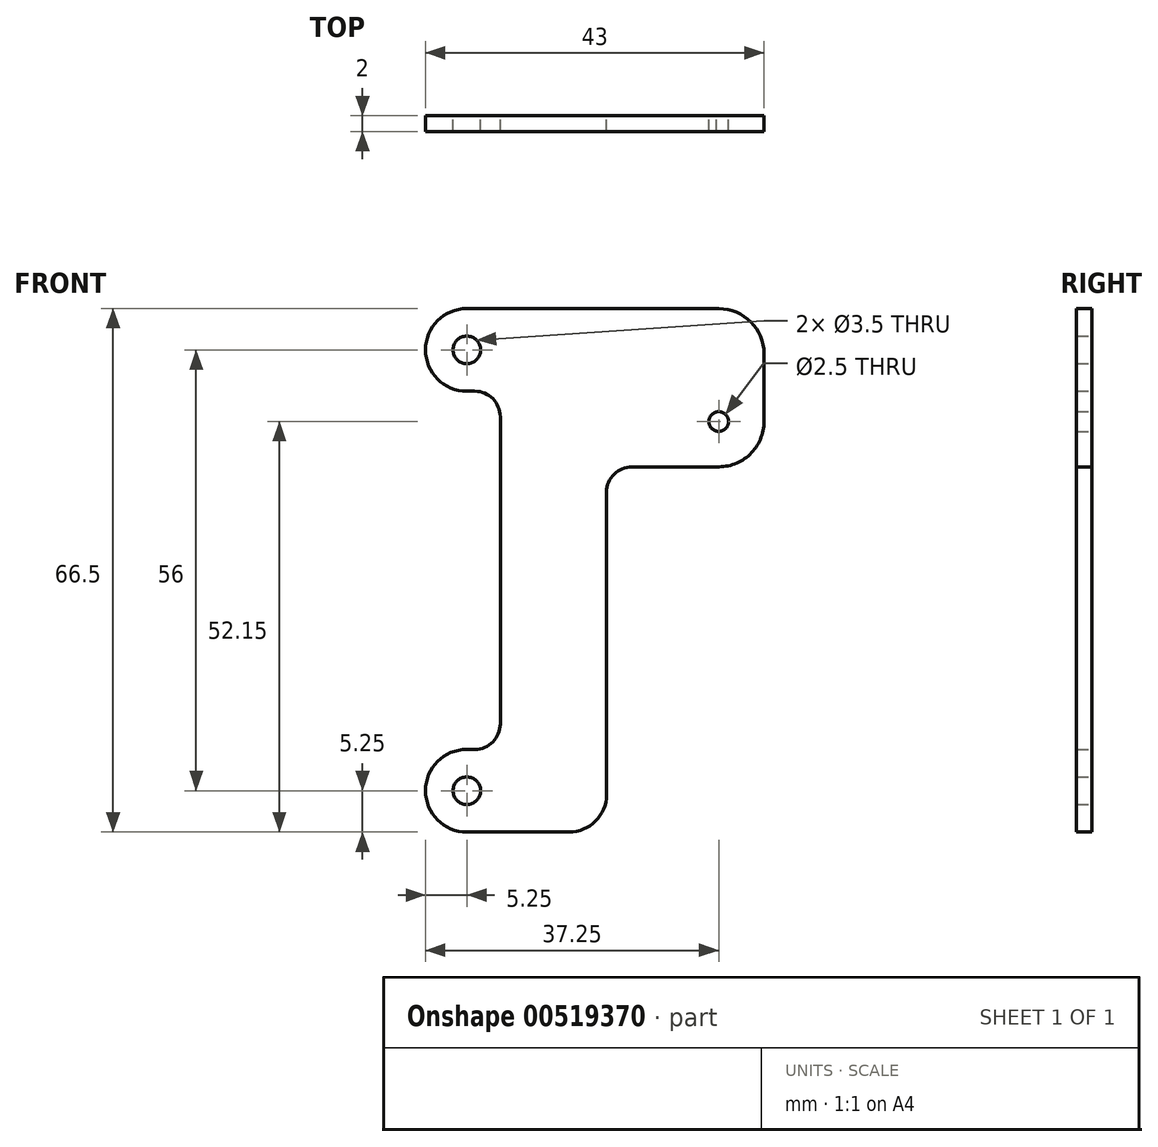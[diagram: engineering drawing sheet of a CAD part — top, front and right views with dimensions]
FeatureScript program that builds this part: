
annotation { "Feature Type Name" : "Feature", "Feature Type Description" : "" }
export const myFeature = defineFeature(function(context is Context, id is Id, definition is map)
    precondition{}
    {
        {
            var Q0;
            Q0=qCreatedBy(makeId("Front.planeOp"),FACE);
            var sketch = newSketch(context, id + "F0", { "sketchPlane" : qUnion([Q0])});
            skArc(sketch, "E0.0", {"start": v(0, 61.25) * mm, "mid": v(-5.25, 56) * mm, "end": v(0, 50.75) * mm});
            skLineSegment(sketch, "E0.1", {"start": v(0, 61.25) * mm, "end": v(32, 61.25) * mm});
            skArc(sketch, "E0.2", {"start": v(37.75, 55.5) * mm, "mid": v(36.07, 59.57) * mm, "end": v(32, 61.25) * mm});
            skLineSegment(sketch, "E0.3", {"start": v(37.75, 55.5) * mm, "end": v(37.75, 46.9) * mm});
            skArc(sketch, "E0.4", {"start": v(0, 5.25) * mm, "mid": v(-5.25, 0) * mm, "end": v(0, -5.25) * mm});
            skLineSegment(sketch, "E0.5", {"start": v(0, 5.25) * mm, "end": v(1, 5.25) * mm});
            skArc(sketch, "E0.6", {"start": v(1, 5.25) * mm, "mid": v(3.3, 6.2) * mm, "end": v(4.25, 8.5) * mm});
            skLineSegment(sketch, "E0.7", {"start": v(4.25, 47.5) * mm, "end": v(4.25, 8.5) * mm});
            skLineSegment(sketch, "E0.8", {"start": v(0, -5.25) * mm, "end": v(13, -5.25) * mm});
            skArc(sketch, "E0.9", {"start": v(13, -5.25) * mm, "mid": v(16.36, -3.86) * mm, "end": v(17.75, -0.5) * mm});
            skLineSegment(sketch, "E0.10", {"start": v(17.75, -0.5) * mm, "end": v(17.75, 37.9) * mm});
            skArc(sketch, "E0.11", {"start": v(21, 41.16) * mm, "mid": v(18.7, 40.2) * mm, "end": v(17.75, 37.9) * mm});
            skLineSegment(sketch, "E0.12", {"start": v(31.74, 41.16) * mm, "end": v(21, 41.16) * mm});
            skArc(sketch, "E0.13", {"start": v(31.74, 41.16) * mm, "mid": v(35.97, 42.74) * mm, "end": v(37.75, 46.9) * mm});
            skArc(sketch, "E1.0", {"start": v(4.25, 47.5) * mm, "mid": v(3.3, 49.8) * mm, "end": v(1, 50.75) * mm});
            skLineSegment(sketch, "E1.1", {"start": v(0, 50.75) * mm, "end": v(1, 50.75) * mm});
            skCircle(sketch, "E2.0", {"center": v(0, 0) * mm, "radius": 1.75 * mm});
            skCircle(sketch, "E3.0", {"center": v(0, 56) * mm, "radius": 1.75 * mm});
            skCircle(sketch, "E4.0", {"center": v(32, 46.9) * mm, "radius": 1.25 * mm});
            skSolve(sketch);
        }
        {
            var Q0;
            Q0 = qSketchRegion(id + "F0", true);
            extrude(context, id + "F1", {"entities" : qUnion([Q0]), "depth" : 2 * mm, "offsetDistance" : 25 * mm});
        }
    });
